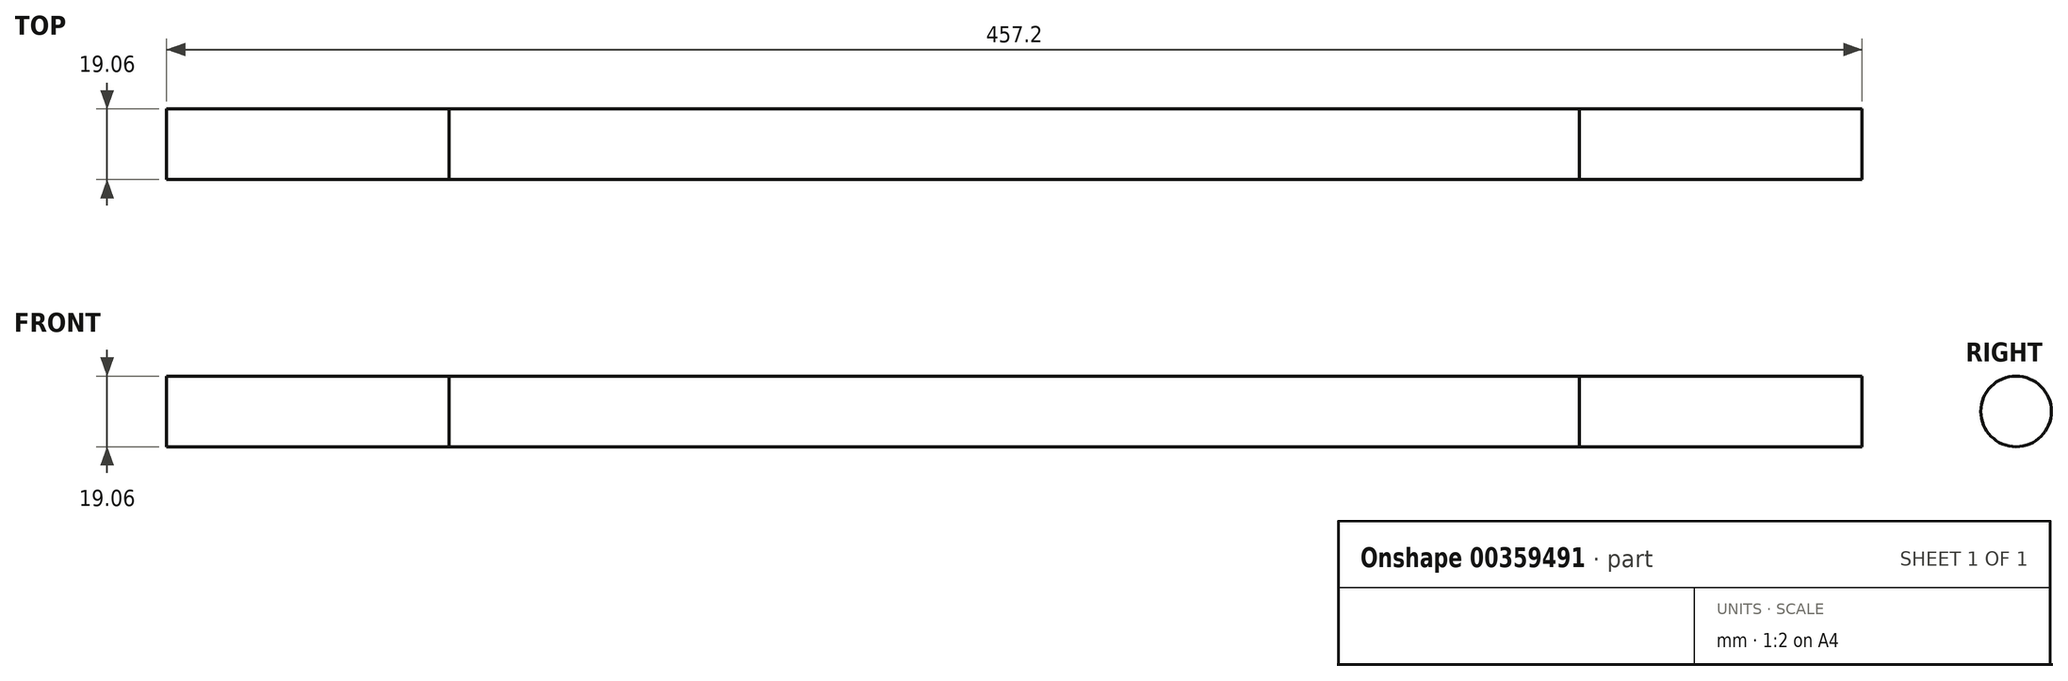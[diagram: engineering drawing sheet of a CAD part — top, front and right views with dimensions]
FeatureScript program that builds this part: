
annotation { "Feature Type Name" : "Feature", "Feature Type Description" : "" }
export const myFeature = defineFeature(function(context is Context, id is Id, definition is map)
    precondition{}
    {
        {
            var Q0;
            Q0=qCreatedBy(makeId("Right.planeOp"),FACE);
            var sketch = newSketch(context, id + "F0", { "sketchPlane" : qUnion([Q0])});
            skCircle(sketch, "E0", {"center": v(0, 0) * mm, "radius": 9.53 * mm});
            skSolve(sketch);
        }
        {
            var Q0;
            Q0=makeQuery(id+"F0.imprint","IMPRINT",FACE,{"disambiguationData":[TD([[makeQuery(id+"F0.imprint","IMPRINT",EDGE,{"derivedFrom":sQuery(id+"F0.wireOp",EDGE,"E0")}),1.0]])]});
            extrude(context, id + "F1", {"entities" : qUnion([Q0]), "endBound" : BoundingType.SYMMETRIC, "depth" : 457.2 * mm});
        }
        {
            var Q0;
            Q0=makeQuery(id+"F0.imprint","IMPRINT",FACE,{"disambiguationData":[TD([[makeQuery(id+"F0.imprint","IMPRINT",EDGE,{"derivedFrom":sQuery(id+"F0.wireOp",EDGE,"E0")}),1.0]])]});
            extrude(context, id + "F2", {"entities" : qUnion([Q0]), "endBound" : BoundingType.SYMMETRIC, "depth" : 304.8 * mm});
        }
    });
